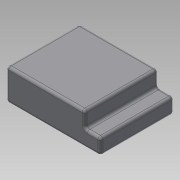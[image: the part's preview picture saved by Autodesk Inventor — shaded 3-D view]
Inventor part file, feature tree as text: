
AUTODESK INVENTOR PART (.ipt)
format: ipt  version: 2015 SP1 (Build 190203100, 203)  size: 126,464 bytes
history: native  units: mm
features: extrude x2, sketch x2, fillet x1
ambient origin geometry x8: Origin, YZ Plane, XZ Plane, XY Plane, X Axis, Y Axis, Z Axis, Center Point
bodies: Solid1 (feature_tree)
feature tree (5):
  extrude  "Extrusion1"  Depth=14.0mm
  extrude  "Extrusion2"  Depth=0.5mm
  fillet  "Fillet1"  Radius=3.0mm
  sketch  "Sketch1"  dims[d0=18.0mm d1=14.0mm]
  sketch  "Sketch2"  dims[d2=6.0mm d3=0.0mm d4=0.5mm d5=3.0mm d6=3.0mm d7=10.0mm d8=0.0mm]
